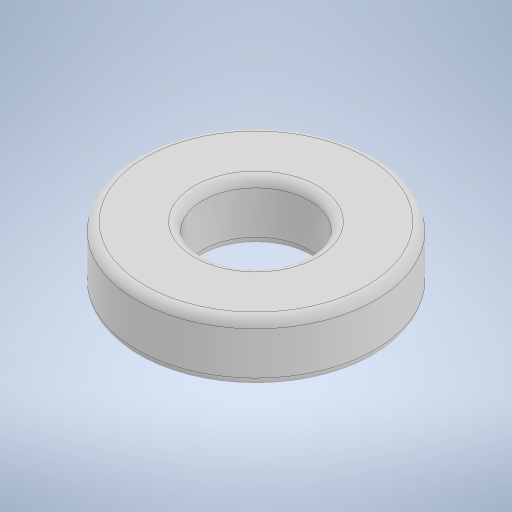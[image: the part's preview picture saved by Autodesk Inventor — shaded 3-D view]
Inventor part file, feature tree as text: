
AUTODESK INVENTOR PART (.ipt)
format: ipt  version: 2023 (Build 270158000, 158)  size: 249,856 bytes
history: native  units: mm
features: fillet x2, extrude x1, sketch x1
ambient origin geometry x8: Origin, YZ Plane, XZ Plane, XY Plane, X Axis, Y Axis, Z Axis, Center Point
bodies: Solid1 (feature_tree)
feature tree (4):
  extrude  "Extrusion1"  Depth=1.0mm
  fillet  "Fillet1"  Radius=7.0mm
  fillet  "Fillet2"  Radius=1.0mm
  sketch  "Sketch1"  dims[d0=12.5mm d1=28.0mm d2=7.0mm d3=0.0mm d4=1.0mm d5=1.0mm]
